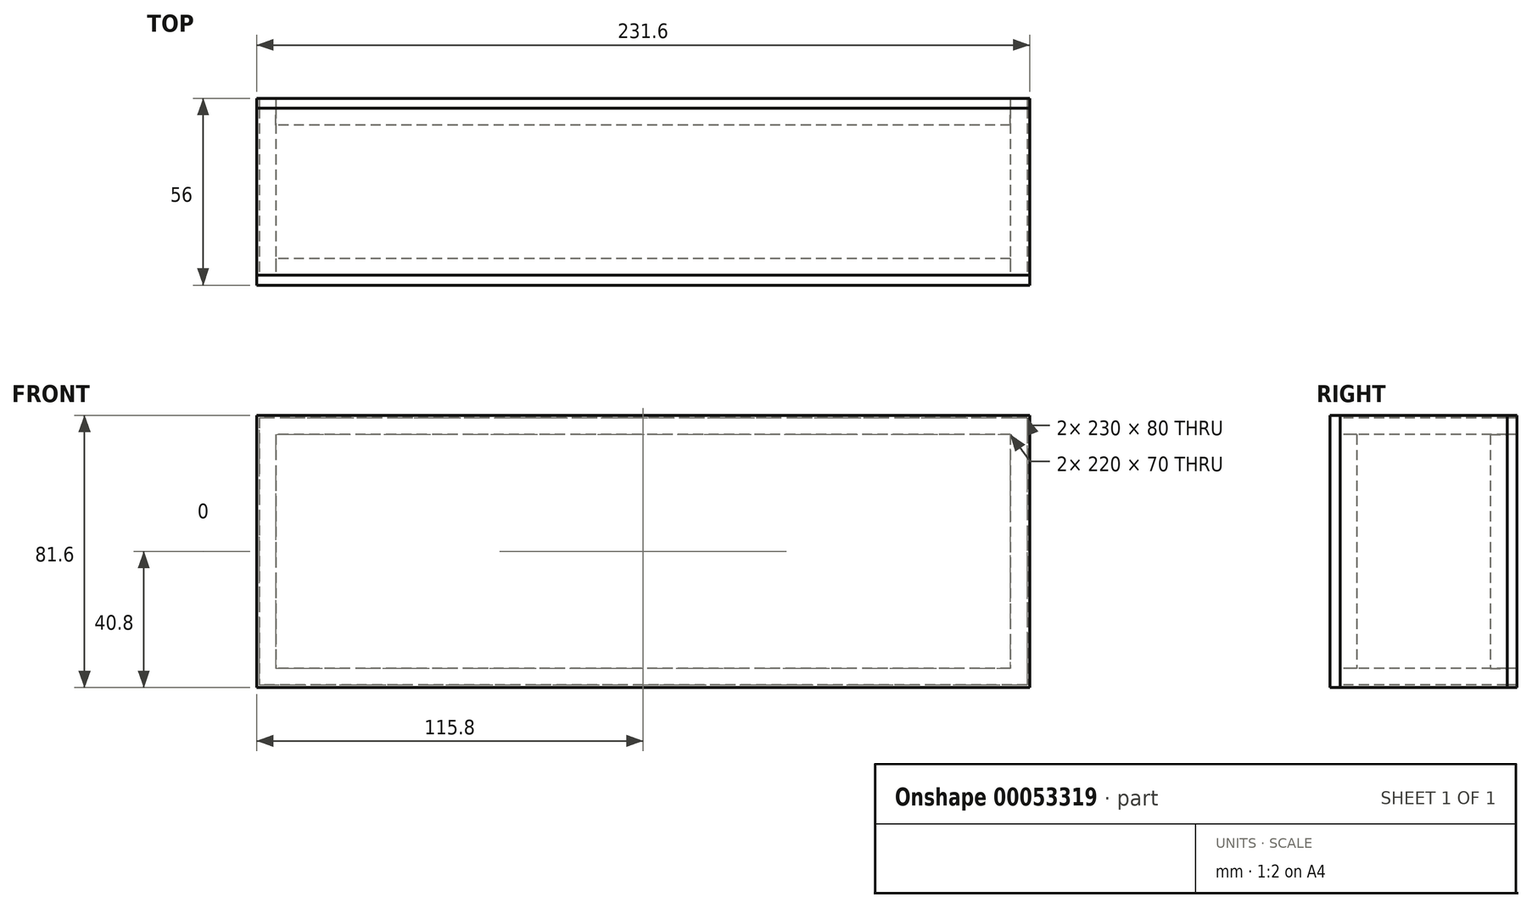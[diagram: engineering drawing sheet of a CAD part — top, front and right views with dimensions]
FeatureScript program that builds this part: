
annotation { "Feature Type Name" : "Feature", "Feature Type Description" : "" }
export const myFeature = defineFeature(function(context is Context, id is Id, definition is map)
    precondition{}
    {
        {
            var Q0;
            Q0=qCreatedBy(makeId("Front.planeOp"),FACE);
            var sketch = newSketch(context, id + "F0", { "sketchPlane" : qUnion([Q0])});
            skLineSegment(sketch, "E0.rect.bottom", {"start": v(110, 35) * mm, "end": v(-110, 35) * mm});
            skLineSegment(sketch, "E0.rect.top", {"start": v(110, -35) * mm, "end": v(-110, -35) * mm});
            skLineSegment(sketch, "E0.rect.left", {"start": v(110, 35) * mm, "end": v(110, -35) * mm});
            skLineSegment(sketch, "E0.rect.right", {"start": v(-110, 35) * mm, "end": v(-110, -35) * mm});
            skPoint(sketch, "E0.rect.middle", {"position": v(0, 0) * mm});
            skLineSegment(sketch, "E1.rect.bottom", {"start": v(115, 40) * mm, "end": v(-115, 40) * mm});
            skLineSegment(sketch, "E1.rect.top", {"start": v(115, -40) * mm, "end": v(-115, -40) * mm});
            skLineSegment(sketch, "E1.rect.left", {"start": v(115, 40) * mm, "end": v(115, -40) * mm});
            skLineSegment(sketch, "E1.rect.right", {"start": v(-115, 40) * mm, "end": v(-115, -40) * mm});
            skLineSegment(sketch, "E2.rect.bottom", {"start": v(115.8, 40.8) * mm, "end": v(-115.8, 40.8) * mm});
            skLineSegment(sketch, "E2.rect.top", {"start": v(115.8, -40.8) * mm, "end": v(-115.8, -40.8) * mm});
            skLineSegment(sketch, "E2.rect.left", {"start": v(115.8, 40.8) * mm, "end": v(115.8, -40.8) * mm});
            skLineSegment(sketch, "E2.rect.right", {"start": v(-115.8, 40.8) * mm, "end": v(-115.8, -40.8) * mm});
            skSolve(sketch);
        }
        {
            var Q0;
            Q0=makeQuery(id+"F0.imprint","IMPRINT",FACE,{"disambiguationData":[TD([[makeQuery(id+"F0.imprint","IMPRINT",EDGE,{"derivedFrom":sQuery(id+"F0.wireOp",EDGE,"E0.rect.bottom")}),-1.0]])]});
            extrude(context, id + "F1", {"entities" : qUnion([Q0]), "oppositeDirection" : true, "depth" : 50 * mm});
        }
        {
            var Q0;
            Q0=makeQuery(id+"F0.imprint","IMPRINT",FACE,{"disambiguationData":[TD([[makeQuery(id+"F0.imprint","IMPRINT",EDGE,{"derivedFrom":sQuery(id+"F0.wireOp",EDGE,"E0.rect.bottom")}),1.0]])]});
            extrude(context, id + "F2", {"entities" : qUnion([Q0]), "oppositeDirection" : true, "depth" : 5 * mm});
        }
        {
            var Q0;
            Q0=makeQuery(id+"F0.imprint","IMPRINT",FACE,{"disambiguationData":[TD([[makeQuery(id+"F0.imprint","IMPRINT",EDGE,{"derivedFrom":sQuery(id+"F0.wireOp",EDGE,"E0.rect.bottom")}),1.0]])]});
            var Q1;
            Q1=makeQuery(id+"F0.imprint","IMPRINT",FACE,{"disambiguationData":[TD([[makeQuery(id+"F0.imprint","IMPRINT",EDGE,{"derivedFrom":sQuery(id+"F0.wireOp",EDGE,"E0.rect.bottom")}),-1.0]])]});
            var Q2;
            Q2=makeQuery(id+"F0.imprint","IMPRINT",FACE,{"disambiguationData":[TD([[makeQuery(id+"F0.imprint","IMPRINT",EDGE,{"derivedFrom":sQuery(id+"F0.wireOp",EDGE,"E1.rect.bottom")}),-1.0]])]});
            extrude(context, id + "F3", {"entities" : qUnion([Q0, Q1, Q2]), "depth" : 3 * mm});
        }
        {
            var Q0;
            Q0=makeQuery(id+"F0.imprint","IMPRINT",FACE,{"disambiguationData":[TD([[makeQuery(id+"F0.imprint","IMPRINT",EDGE,{"derivedFrom":sQuery(id+"F0.wireOp",EDGE,"E1.rect.bottom")}),-1.0]])]});
            extrude(context, id + "F4", {"entities" : qUnion([Q0]), "oppositeDirection" : true, "depth" : 50 * mm});
        }
        {
            var Q0;
            Q0=makeQuery(id+"F1.opExtrude","CAP_FACE",FACE,{"disambiguationData":[OSD([sQuery(id+"F0.wireOp",EDGE,"E0.rect.bottom"),sQuery(id+"F0.wireOp",EDGE,"E0.rect.top"),sQuery(id+"F0.wireOp",EDGE,"E0.rect.left"),sQuery(id+"F0.wireOp",EDGE,"E0.rect.right"),sQuery(id+"F0.wireOp",EDGE,"E1.rect.bottom"),sQuery(id+"F0.wireOp",EDGE,"E1.rect.top"),sQuery(id+"F0.wireOp",EDGE,"E1.rect.left"),sQuery(id+"F0.wireOp",EDGE,"E1.rect.right")])],"isStart":false});
            var sketch = newSketch(context, id + "F5", { "sketchPlane" : qUnion([Q0])});
            skLineSegment(sketch, "E3.bottom", {"start": v(-110, 35) * mm, "end": v(110, 35) * mm});
            skLineSegment(sketch, "E3.top", {"start": v(-110, -35) * mm, "end": v(110, -35) * mm});
            skLineSegment(sketch, "E3.left", {"start": v(-110, 35) * mm, "end": v(-110, -35) * mm});
            skLineSegment(sketch, "E3.right", {"start": v(110, 35) * mm, "end": v(110, -35) * mm});
            skSolve(sketch);
        }
        {
            var Q0;
            Q0=makeQuery(id+"F5.imprint","IMPRINT",FACE,{"disambiguationData":[TD([[makeQuery(id+"F5.imprint","IMPRINT",EDGE,{"derivedFrom":sQuery(id+"F5.wireOp",EDGE,"E3.bottom")}),-1.0]])]});
            extrude(context, id + "F6", {"entities" : qUnion([Q0]), "oppositeDirection" : true, "depth" : 5 * mm});
        }
        {
            var Q0;
            Q0=makeQuery(id+"F4.opExtrude","CAP_FACE",FACE,{"disambiguationData":[OSD([sQuery(id+"F0.wireOp",EDGE,"E1.rect.bottom"),sQuery(id+"F0.wireOp",EDGE,"E1.rect.top"),sQuery(id+"F0.wireOp",EDGE,"E1.rect.left"),sQuery(id+"F0.wireOp",EDGE,"E1.rect.right"),sQuery(id+"F0.wireOp",EDGE,"E2.rect.bottom"),sQuery(id+"F0.wireOp",EDGE,"E2.rect.top"),sQuery(id+"F0.wireOp",EDGE,"E2.rect.left"),sQuery(id+"F0.wireOp",EDGE,"E2.rect.right")])],"isStart":false});
            var Q1;
            Q1=makeQuery(id+"F1.opExtrude","CAP_FACE",FACE,{"disambiguationData":[OSD([sQuery(id+"F0.wireOp",EDGE,"E0.rect.bottom"),sQuery(id+"F0.wireOp",EDGE,"E0.rect.top"),sQuery(id+"F0.wireOp",EDGE,"E0.rect.left"),sQuery(id+"F0.wireOp",EDGE,"E0.rect.right"),sQuery(id+"F0.wireOp",EDGE,"E1.rect.bottom"),sQuery(id+"F0.wireOp",EDGE,"E1.rect.top"),sQuery(id+"F0.wireOp",EDGE,"E1.rect.left"),sQuery(id+"F0.wireOp",EDGE,"E1.rect.right")])],"isStart":false});
            var Q2;
            Q2=makeQuery(id+"F6.opExtrude","CAP_FACE",FACE,{"disambiguationData":[OSD([sQuery(id+"F5.wireOp",EDGE,"E3.bottom"),sQuery(id+"F5.wireOp",EDGE,"E3.top"),sQuery(id+"F5.wireOp",EDGE,"E3.left"),sQuery(id+"F5.wireOp",EDGE,"E3.right")])],"isStart":true});
            extrude(context, id + "F7", {"entities" : qUnion([Q0, Q1, Q2]), "depth" : 3 * mm});
        }
    });
